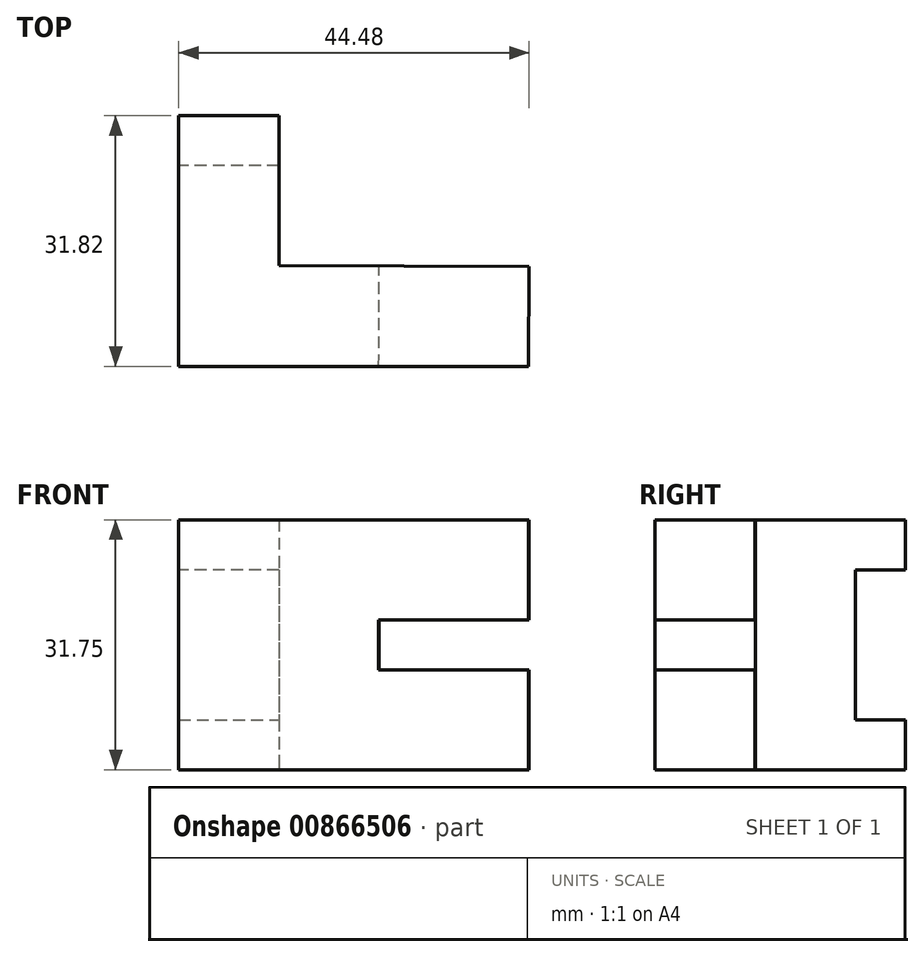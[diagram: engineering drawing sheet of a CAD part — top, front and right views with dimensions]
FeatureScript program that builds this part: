
annotation { "Feature Type Name" : "Feature", "Feature Type Description" : "" }
export const myFeature = defineFeature(function(context is Context, id is Id, definition is map)
    precondition{}
    {
        {
            var Q0;
            Q0=qCreatedBy(makeId("Top.planeOp"),FACE);
            var sketch = newSketch(context, id + "F0", { "sketchPlane" : qUnion([Q0])});
            skLineSegment(sketch, "E0", {"start": v(-31.75, 19.12) * mm, "end": v(-31.75, 0.07) * mm});
            skLineSegment(sketch, "E1", {"start": v(-31.75, 0.07) * mm, "end": v(0, 0) * mm});
            skLineSegment(sketch, "E2", {"start": v(0, 0) * mm, "end": v(-0.03, -12.7) * mm});
            skLineSegment(sketch, "E3", {"start": v(-0.03, -12.7) * mm, "end": v(-44.48, -12.7) * mm});
            skLineSegment(sketch, "E4", {"start": v(-44.48, -12.7) * mm, "end": v(-44.48, 19.12) * mm});
            skLineSegment(sketch, "E5", {"start": v(-44.48, 19.12) * mm, "end": v(-31.75, 19.12) * mm});
            skSolve(sketch);
        }
        {
            var Q0;
            Q0 = qSketchRegion(id + "F0", true);
            extrude(context, id + "F1", {"entities" : qUnion([Q0]), "depth" : 31.75 * mm, "offsetDistance" : 25.4 * mm});
        }
        {
            var Q0;
            Q0=makeQuery(id+"F1.opExtrude","SWEPT_FACE",FACE,{"disambiguationData":[OSD([sQuery(id+"F0.wireOp",EDGE,"E5")])]});
            var sketch = newSketch(context, id + "F2", { "sketchPlane" : qUnion([Q0])});
            skLineSegment(sketch, "E6", {"start": v(31.75, 25.4) * mm, "end": v(44.48, 25.4) * mm});
            skLineSegment(sketch, "E7", {"start": v(44.48, 25.4) * mm, "end": v(44.48, 6.35) * mm});
            skLineSegment(sketch, "E8", {"start": v(44.48, 6.35) * mm, "end": v(31.75, 6.35) * mm});
            skLineSegment(sketch, "E9", {"start": v(31.75, 6.35) * mm, "end": v(31.75, 25.4) * mm});
            skSolve(sketch);
        }
        {
            var Q0;
            Q0 = qSketchRegion(id + "F2", true);
            extrude(context, id + "F3", {"entities" : qUnion([Q0]), "operationType" : NewBodyOperationType.REMOVE, "oppositeDirection" : true, "depth" : 6.35 * mm, "offsetDistance" : 25.4 * mm});
        }
        {
            var Q0;
            Q0=makeQuery(id+"F1.opExtrude","SWEPT_FACE",FACE,{"disambiguationData":[OSD([sQuery(id+"F0.wireOp",EDGE,"E1")])]});
            var sketch = newSketch(context, id + "F4", { "sketchPlane" : qUnion([Q0])});
            skLineSegment(sketch, "E10.bottom", {"start": v(0, 19.05) * mm, "end": v(19.05, 19.05) * mm});
            skLineSegment(sketch, "E10.top", {"start": v(0, 12.7) * mm, "end": v(19.05, 12.7) * mm});
            skLineSegment(sketch, "E10.left", {"start": v(0, 19.05) * mm, "end": v(0, 12.7) * mm});
            skLineSegment(sketch, "E10.right", {"start": v(19.05, 19.05) * mm, "end": v(19.05, 12.7) * mm});
            skSolve(sketch);
        }
        {
            var Q0;
            Q0=makeQuery(id+"F4.imprint","IMPRINT",FACE,{"disambiguationData":[TD([[makeQuery(id+"F4.imprint","IMPRINT",EDGE,{"derivedFrom":sQuery(id+"F4.wireOp",EDGE,"E10.bottom")}),-1.0]])]});
            var Q1;
            Q1=sQuery(id+"F4.wireOp",EDGE,"E10.top");
            extrude(context, id + "F5", {"entities" : qUnion([Q0]), "operationType" : NewBodyOperationType.REMOVE, "surfaceEntities" : qUnion([Q1]), "oppositeDirection" : true, "depth" : 14.45 * mm, "offsetDistance" : 25.4 * mm});
        }
    });
